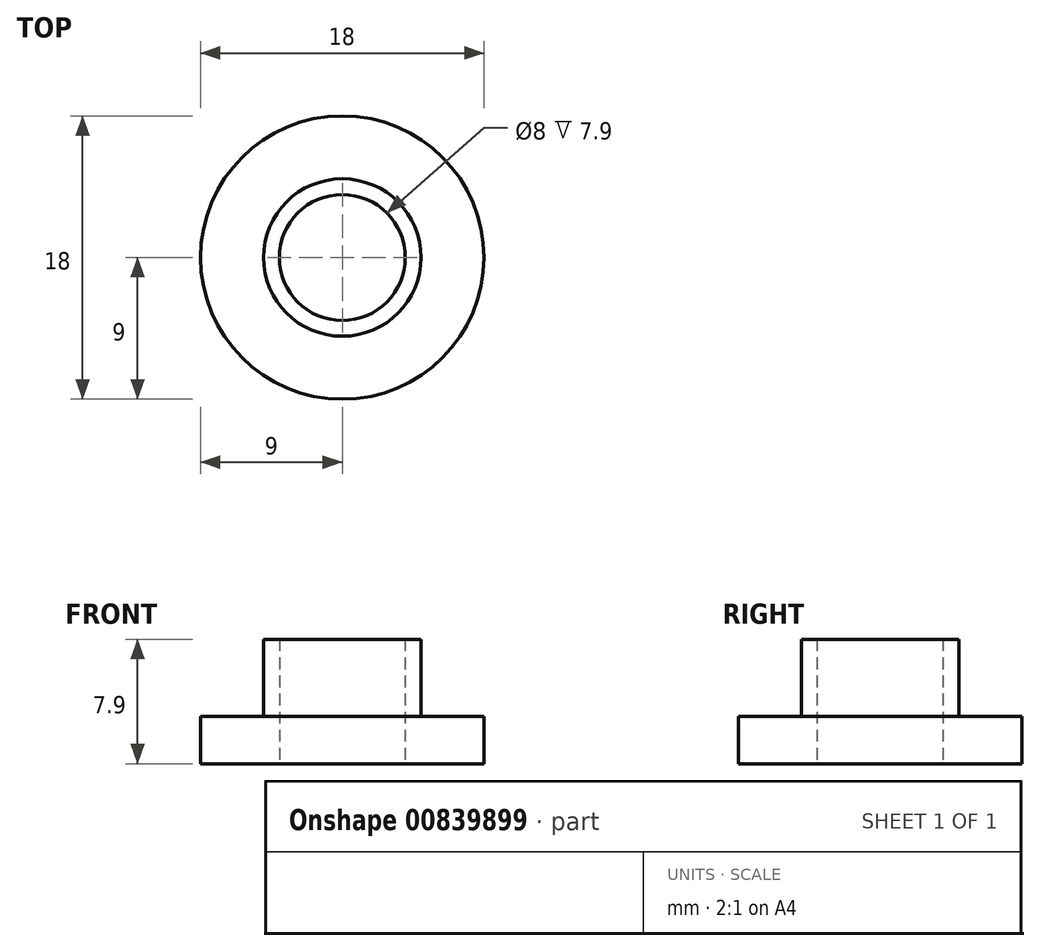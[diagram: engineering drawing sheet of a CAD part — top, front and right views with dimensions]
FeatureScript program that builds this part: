
annotation { "Feature Type Name" : "Feature", "Feature Type Description" : "" }
export const myFeature = defineFeature(function(context is Context, id is Id, definition is map)
    precondition{}
    {
        {
            var Q0;
            Q0=qCreatedBy(makeId("Top.planeOp"),FACE);
            var sketch = newSketch(context, id + "F0", { "sketchPlane" : qUnion([Q0])});
            skCircle(sketch, "E0", {"center": v(0, 0) * mm, "radius": 9 * mm});
            skSolve(sketch);
        }
        {
            var Q0;
            Q0 = qSketchRegion(id + "F0", true);
            extrude(context, id + "F1", {"entities" : qUnion([Q0]), "oppositeDirection" : true, "depth" : 3 * mm, "offsetDistance" : 25 * mm});
        }
        {
            var Q0;
            Q0=qCreatedBy(makeId("Top.planeOp"),FACE);
            var sketch = newSketch(context, id + "F2", { "sketchPlane" : qUnion([Q0])});
            skCircle(sketch, "E1", {"center": v(0, 0) * mm, "radius": 5 * mm});
            skSolve(sketch);
        }
        {
            var Q0;
            Q0 = qSketchRegion(id + "F2", true);
            extrude(context, id + "F3", {"entities" : qUnion([Q0]), "operationType" : NewBodyOperationType.ADD, "depth" : 4.9 * mm, "offsetDistance" : 25 * mm});
        }
        {
            var Q0;
            Q0=qCreatedBy(makeId("Top.planeOp"),FACE);
            var sketch = newSketch(context, id + "F4", { "sketchPlane" : qUnion([Q0])});
            skCircle(sketch, "E2", {"center": v(0, 0) * mm, "radius": 4 * mm});
            skSolve(sketch);
        }
        {
            var Q0;
            Q0 = qSketchRegion(id + "F4", true);
            extrude(context, id + "F5", {"entities" : qUnion([Q0]), "operationType" : NewBodyOperationType.REMOVE, "endBound" : BoundingType.SYMMETRIC, "depth" : 30 * mm, "offsetDistance" : 25 * mm});
        }
    });
